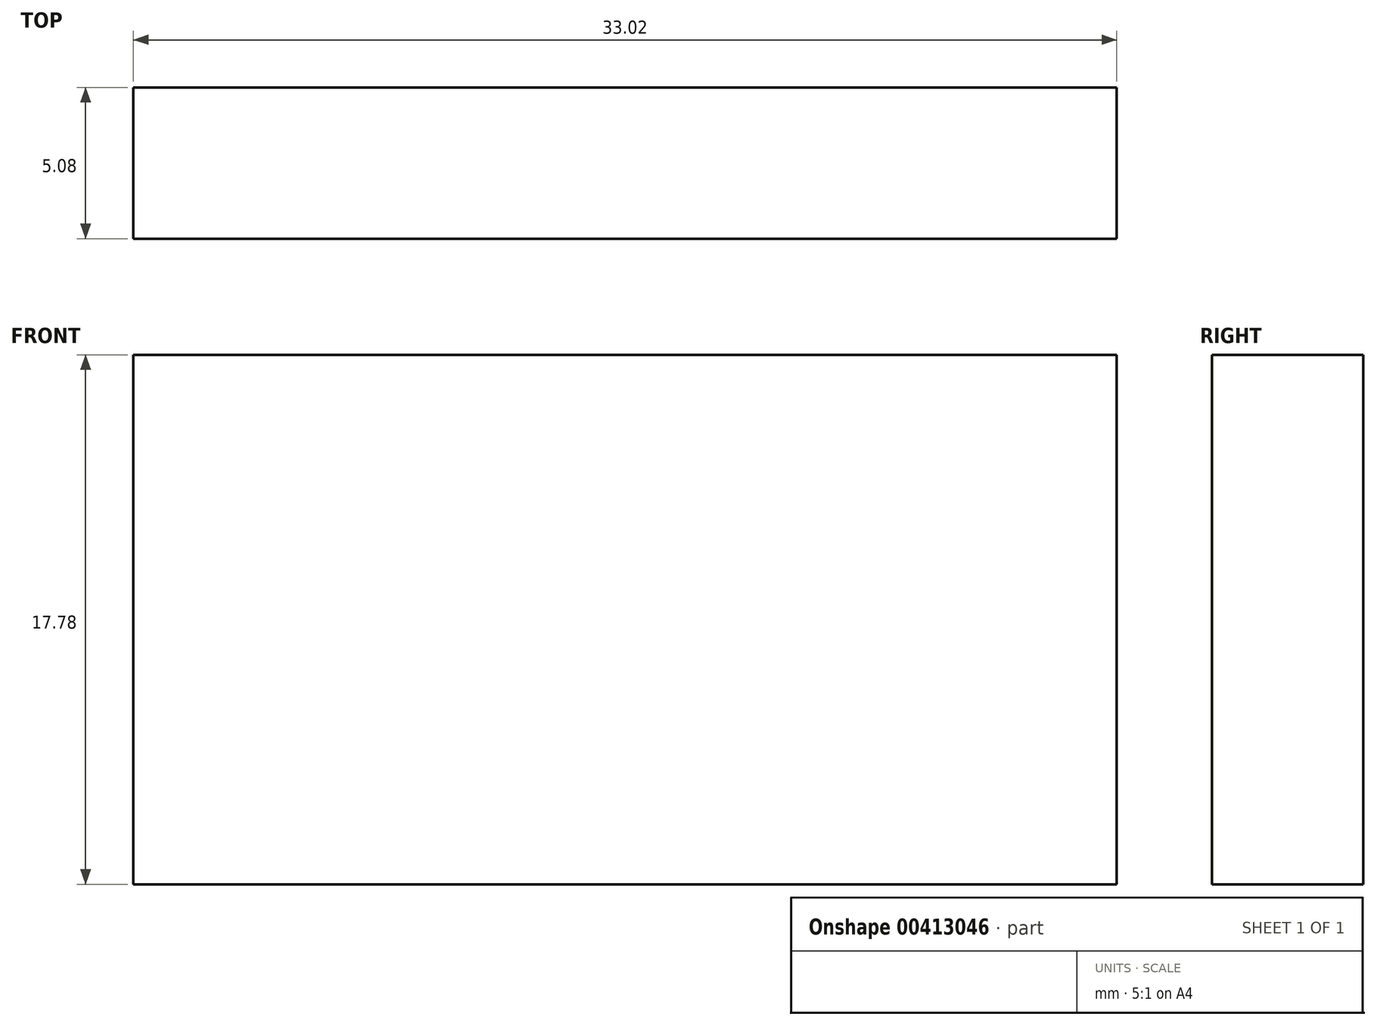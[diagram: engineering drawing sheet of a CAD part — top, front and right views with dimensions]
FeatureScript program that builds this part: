
annotation { "Feature Type Name" : "Feature", "Feature Type Description" : "" }
export const myFeature = defineFeature(function(context is Context, id is Id, definition is map)
    precondition{}
    {
        {
            var Q0;
            Q0=qCreatedBy(makeId("Front.planeOp"),FACE);
            var sketch = newSketch(context, id + "F0", { "sketchPlane" : qUnion([Q0])});
            skLineSegment(sketch, "E0.bottom", {"start": v(0, 0) * mm, "end": v(33.02, 0) * mm});
            skLineSegment(sketch, "E0.top", {"start": v(0, 17.78) * mm, "end": v(33.02, 17.78) * mm});
            skLineSegment(sketch, "E0.left", {"start": v(0, 0) * mm, "end": v(0, 17.78) * mm});
            skLineSegment(sketch, "E0.right", {"start": v(33.02, 0) * mm, "end": v(33.02, 17.78) * mm});
            skSolve(sketch);
        }
        {
            var Q0;
            Q0 = qSketchRegion(id + "F0", true);
            extrude(context, id + "F1", {"entities" : qUnion([Q0]), "depth" : 5.08 * mm});
        }
    });
